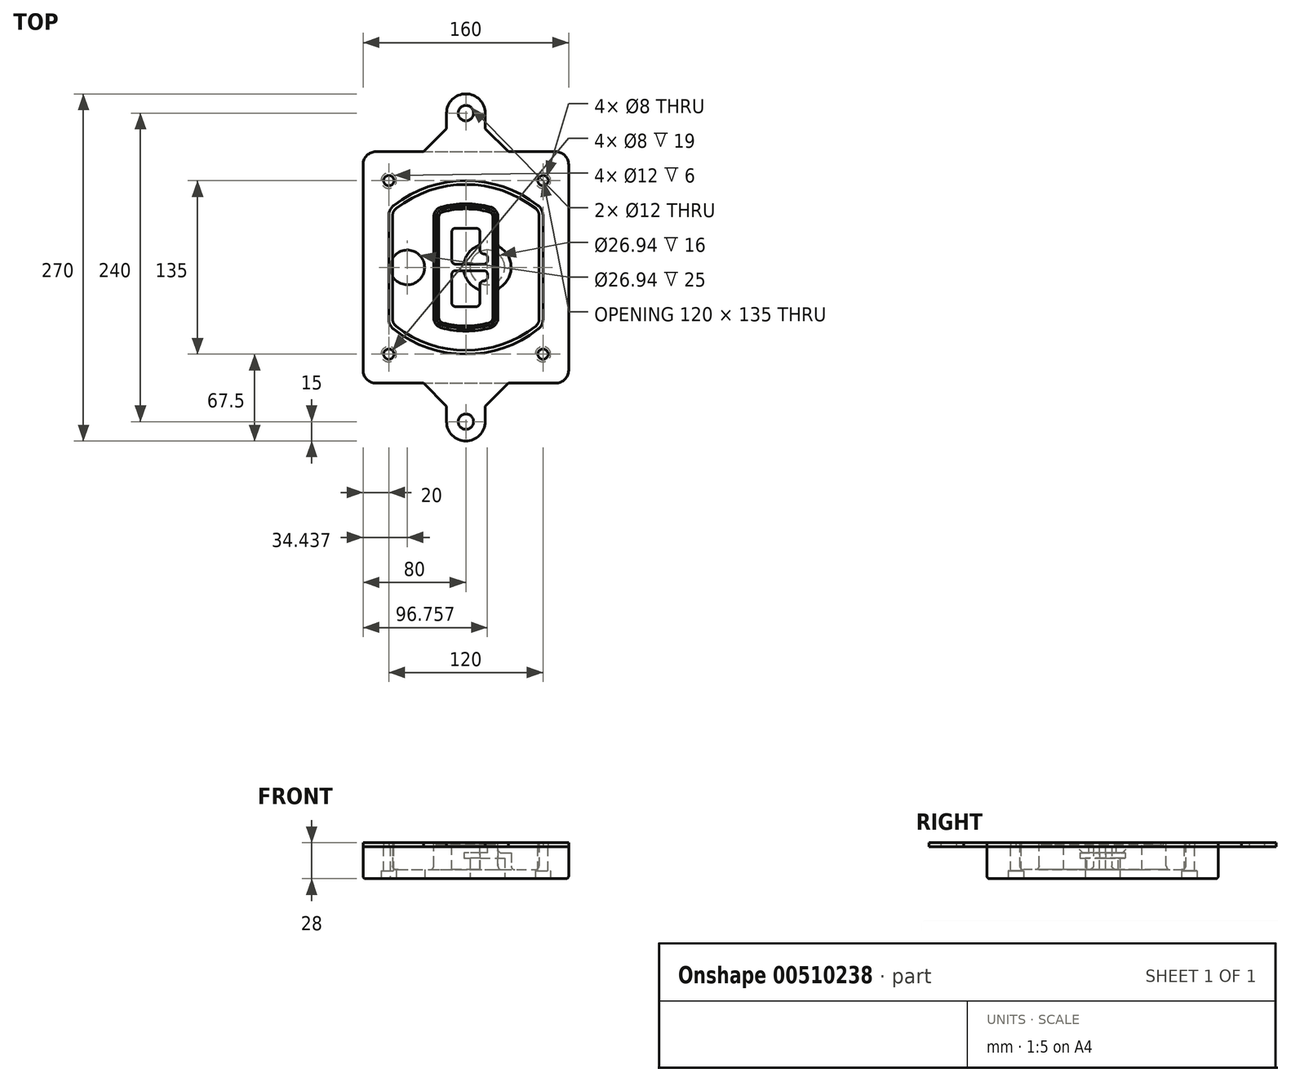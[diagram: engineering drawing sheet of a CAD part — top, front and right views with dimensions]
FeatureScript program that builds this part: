
annotation { "Feature Type Name" : "Feature", "Feature Type Description" : "" }
export const myFeature = defineFeature(function(context is Context, id is Id, definition is map)
    precondition{}
    {
        {
            var Q0;
            Q0=qCreatedBy(makeId("Top.planeOp"),FACE);
            var sketch = newSketch(context, id + "F0", { "sketchPlane" : qUnion([Q0])});
            skPoint(sketch, "E0.rect.middle", {"position": v(0, 0) * mm});
            skLineSegment(sketch, "E1.bottom", {"start": v(-70, -90) * mm, "end": v(70, -90) * mm});
            skLineSegment(sketch, "E1.top", {"start": v(-70, 90) * mm, "end": v(70, 90) * mm});
            skLineSegment(sketch, "E1.left", {"start": v(-80, -80) * mm, "end": v(-80, 80) * mm});
            skLineSegment(sketch, "E1.right", {"start": v(80, -80) * mm, "end": v(80, 80) * mm});
            skLineSegment(sketch, "E2", {"start": v(-80, 90) * mm, "end": v(80, -90) * mm, "construction": true});
            skLineSegment(sketch, "E3", {"start": v(80, 90) * mm, "end": v(-80, -90) * mm, "construction": true});
            skCircle(sketch, "E4", {"center": v(-60, 67.5) * mm, "radius": 4 * mm});
            skCircle(sketch, "E5", {"center": v(60, 67.5) * mm, "radius": 4 * mm});
            skCircle(sketch, "E6", {"center": v(60, -67.5) * mm, "radius": 4 * mm});
            skCircle(sketch, "E7", {"center": v(-60, -67.5) * mm, "radius": 4 * mm});
            skLineSegment(sketch, "E8", {"start": v(-60, 67.5) * mm, "end": v(60, 67.5) * mm, "construction": true});
            skLineSegment(sketch, "E9", {"start": v(60, 67.5) * mm, "end": v(60, -67.5) * mm, "construction": true});
            skLineSegment(sketch, "E10", {"start": v(60, -67.5) * mm, "end": v(-60, -67.5) * mm, "construction": true});
            skLineSegment(sketch, "E11", {"start": v(-60, -67.5) * mm, "end": v(-60, 67.5) * mm, "construction": true});
            skLineSegment(sketch, "E12", {"start": v(-60, 40.3) * mm, "end": v(-60, -40.3) * mm});
            skLineSegment(sketch, "E13", {"start": v(60, 40.3) * mm, "end": v(60, -40.3) * mm});
            skArc(sketch, "E14", {"start": v(56.15, 48.18) * mm, "mid": v(0, 67.5) * mm, "end": v(-56.15, 48.18) * mm});
            skArc(sketch, "E15", {"start": v(-56.15, -48.18) * mm, "mid": v(0, -67.5) * mm, "end": v(56.15, -48.18) * mm});
            skLineSegment(sketch, "E16", {"start": v(-60, 0) * mm, "end": v(60, 0) * mm, "construction": true});
            skPoint(sketch, "E17.visualSharp", {"position": v(-60, -45) * mm});
            skArc(sketch, "E17.filletArc", {"start": v(-60, -40.3) * mm, "mid": v(-58.99, -44.68) * mm, "end": v(-56.15, -48.18) * mm});
            skPoint(sketch, "E18.visualSharp", {"position": v(-60, 45) * mm});
            skArc(sketch, "E18.filletArc", {"start": v(-56.15, 48.18) * mm, "mid": v(-58.99, 44.68) * mm, "end": v(-60, 40.3) * mm});
            skPoint(sketch, "E19.visualSharp", {"position": v(60, 45) * mm});
            skArc(sketch, "E19.filletArc", {"start": v(60, 40.3) * mm, "mid": v(58.99, 44.68) * mm, "end": v(56.15, 48.18) * mm});
            skPoint(sketch, "E20.visualSharp", {"position": v(60, -45) * mm});
            skArc(sketch, "E20.filletArc", {"start": v(56.15, -48.18) * mm, "mid": v(58.99, -44.68) * mm, "end": v(60, -40.3) * mm});
            skPoint(sketch, "E21.visualSharp", {"position": v(-80, 90) * mm});
            skArc(sketch, "E21.filletArc", {"start": v(-70, 90) * mm, "mid": v(-77.07, 87.07) * mm, "end": v(-80, 80) * mm});
            skPoint(sketch, "E22.visualSharp", {"position": v(80, 90) * mm});
            skArc(sketch, "E22.filletArc", {"start": v(80, 80) * mm, "mid": v(77.07, 87.07) * mm, "end": v(70, 90) * mm});
            skPoint(sketch, "E23.visualSharp", {"position": v(80, -90) * mm});
            skArc(sketch, "E23.filletArc", {"start": v(70, -90) * mm, "mid": v(77.07, -87.07) * mm, "end": v(80, -80) * mm});
            skPoint(sketch, "E24.visualSharp", {"position": v(-80, -90) * mm});
            skArc(sketch, "E24.filletArc", {"start": v(-80, -80) * mm, "mid": v(-77.07, -87.07) * mm, "end": v(-70, -90) * mm});
            skArc(sketch, "E25.0", {"start": v(57, 40.3) * mm, "mid": v(56.3, 43.36) * mm, "end": v(54.3, 45.81) * mm});
            skLineSegment(sketch, "E25.1", {"start": v(57, 40.3) * mm, "end": v(57, -40.3) * mm});
            skArc(sketch, "E25.2", {"start": v(54.3, -45.81) * mm, "mid": v(56.3, -43.36) * mm, "end": v(57, -40.3) * mm});
            skArc(sketch, "E25.3", {"start": v(-54.3, -45.81) * mm, "mid": v(0, -64.5) * mm, "end": v(54.3, -45.81) * mm});
            skArc(sketch, "E25.4", {"start": v(-57, -40.3) * mm, "mid": v(-56.3, -43.36) * mm, "end": v(-54.3, -45.81) * mm});
            skArc(sketch, "E25.5", {"start": v(54.3, 45.81) * mm, "mid": v(0, 64.5) * mm, "end": v(-54.3, 45.81) * mm});
            skLineSegment(sketch, "E25.6", {"start": v(-57, 40.3) * mm, "end": v(-57, -40.3) * mm});
            skArc(sketch, "E25.7", {"start": v(-54.3, 45.81) * mm, "mid": v(-56.3, 43.36) * mm, "end": v(-57, 40.3) * mm});
            skArc(sketch, "E26.0", {"start": v(-58.62, 51.33) * mm, "mid": v(-62.58, 46.43) * mm, "end": v(-64, 40.3) * mm});
            skArc(sketch, "E26.1", {"start": v(58.62, 51.33) * mm, "mid": v(0, 71.5) * mm, "end": v(-58.62, 51.33) * mm});
            skArc(sketch, "E26.2", {"start": v(64, 40.3) * mm, "mid": v(62.58, 46.43) * mm, "end": v(58.62, 51.33) * mm});
            skLineSegment(sketch, "E26.3", {"start": v(64, 40.3) * mm, "end": v(64, -40.3) * mm});
            skArc(sketch, "E26.4", {"start": v(58.62, -51.33) * mm, "mid": v(62.58, -46.43) * mm, "end": v(64, -40.3) * mm});
            skLineSegment(sketch, "E26.5", {"start": v(-64, 40.3) * mm, "end": v(-64, -40.3) * mm});
            skArc(sketch, "E26.6", {"start": v(-58.62, -51.33) * mm, "mid": v(0, -71.5) * mm, "end": v(58.62, -51.33) * mm});
            skArc(sketch, "E26.7", {"start": v(-64, -40.3) * mm, "mid": v(-62.58, -46.43) * mm, "end": v(-58.62, -51.33) * mm});
            skSolve(sketch);
        }
        {
            var Q0;
            Q0=makeQuery(id+"F0.imprint","IMPRINT",FACE,{"disambiguationData":[TD([[makeQuery(id+"F0.imprint","IMPRINT",EDGE,{"derivedFrom":sQuery(id+"F0.wireOp",EDGE,"E1.bottom")}),1.0]])]});
            var Q1;
            Q1=makeQuery(id+"F0.imprint","IMPRINT",FACE,{"disambiguationData":[TD([[makeQuery(id+"F0.imprint","IMPRINT",EDGE,{"derivedFrom":sQuery(id+"F0.wireOp",EDGE,"E12")}),1.0]])]});
            var Q2;
            Q2=makeQuery(id+"F0.imprint","IMPRINT",FACE,{"disambiguationData":[TD([[makeQuery(id+"F0.imprint","IMPRINT",EDGE,{"derivedFrom":sQuery(id+"F0.wireOp",EDGE,"E25.0")}),1.0]])]});
            var Q3;
            Q3=makeQuery(id+"F0.imprint","IMPRINT",FACE,{"disambiguationData":[TD([[makeQuery(id+"F0.imprint","IMPRINT",EDGE,{"derivedFrom":sQuery(id+"F0.wireOp",EDGE,"E12")}),-1.0]])]});
            extrude(context, id + "F1", {"entities" : qUnion([Q0, Q1, Q2, Q3]), "oppositeDirection" : true, "depth" : 25 * mm});
        }
        {
            var Q0;
            Q0=makeQuery(id+"F0.imprint","IMPRINT",FACE,{"disambiguationData":[TD([[makeQuery(id+"F0.imprint","IMPRINT",EDGE,{"derivedFrom":sQuery(id+"F0.wireOp",EDGE,"E12")}),1.0]])]});
            extrude(context, id + "F2", {"entities" : qUnion([Q0]), "operationType" : NewBodyOperationType.ADD, "depth" : 3 * mm});
        }
        {
            var Q0;
            Q0=makeQuery(id+"F0.imprint","IMPRINT",FACE,{"disambiguationData":[TD([[makeQuery(id+"F0.imprint","IMPRINT",EDGE,{"derivedFrom":sQuery(id+"F0.wireOp",EDGE,"E25.0")}),1.0]])]});
            extrude(context, id + "F3", {"entities" : qUnion([Q0]), "operationType" : NewBodyOperationType.REMOVE, "oppositeDirection" : true, "depth" : 18 * mm});
        }
        {
            var Q0;
            Q0=makeQuery(id+"F2.opExtrude","CAP_FACE",FACE,{"disambiguationData":[OSD([sQuery(id+"F0.wireOp",EDGE,"E12"),sQuery(id+"F0.wireOp",EDGE,"E13"),sQuery(id+"F0.wireOp",EDGE,"E14"),sQuery(id+"F0.wireOp",EDGE,"E15"),sQuery(id+"F0.wireOp",EDGE,"E17.filletArc"),sQuery(id+"F0.wireOp",EDGE,"E18.filletArc"),sQuery(id+"F0.wireOp",EDGE,"E19.filletArc"),sQuery(id+"F0.wireOp",EDGE,"E20.filletArc"),sQuery(id+"F0.wireOp",EDGE,"E25.0"),sQuery(id+"F0.wireOp",EDGE,"E25.1"),sQuery(id+"F0.wireOp",EDGE,"E25.2"),sQuery(id+"F0.wireOp",EDGE,"E25.3"),sQuery(id+"F0.wireOp",EDGE,"E25.4"),sQuery(id+"F0.wireOp",EDGE,"E25.5"),sQuery(id+"F0.wireOp",EDGE,"E25.6"),sQuery(id+"F0.wireOp",EDGE,"E25.7")])],"isStart":false});
            var sketch = newSketch(context, id + "F4", { "sketchPlane" : qUnion([Q0])});
            skArc(sketch, "E27.0", {"start": v(-19.08, -46.97) * mm, "mid": v(0, -49.5) * mm, "end": v(19.08, -46.97) * mm});
            skArc(sketch, "E28.0", {"start": v(19.08, 46.97) * mm, "mid": v(0, 49.5) * mm, "end": v(-19.08, 46.97) * mm});
            skLineSegment(sketch, "E29", {"start": v(-25, 39.25) * mm, "end": v(-25, -39.25) * mm});
            skLineSegment(sketch, "E30", {"start": v(25, 39.25) * mm, "end": v(25, -39.25) * mm});
            skLineSegment(sketch, "E31", {"start": v(-25, 45.1) * mm, "end": v(25, 45.1) * mm, "construction": true});
            skLineSegment(sketch, "E32", {"start": v(-25, -45.1) * mm, "end": v(25, -45.1) * mm, "construction": true});
            skPoint(sketch, "E33.visualSharp", {"position": v(-25, 45.1) * mm});
            skArc(sketch, "E33.filletArc", {"start": v(-19.08, 46.97) * mm, "mid": v(-23.35, 44.11) * mm, "end": v(-25, 39.25) * mm});
            skPoint(sketch, "E34.visualSharp", {"position": v(25, 45.1) * mm});
            skArc(sketch, "E34.filletArc", {"start": v(25, 39.25) * mm, "mid": v(23.35, 44.11) * mm, "end": v(19.08, 46.97) * mm});
            skPoint(sketch, "E35.visualSharp", {"position": v(25, -45.1) * mm});
            skArc(sketch, "E35.filletArc", {"start": v(19.08, -46.97) * mm, "mid": v(23.35, -44.11) * mm, "end": v(25, -39.25) * mm});
            skPoint(sketch, "E36.visualSharp", {"position": v(-25, -45.1) * mm});
            skArc(sketch, "E36.filletArc", {"start": v(-25, -39.25) * mm, "mid": v(-23.35, -44.11) * mm, "end": v(-19.08, -46.97) * mm});
            skArc(sketch, "E37.0", {"start": v(54.3, 45.81) * mm, "mid": v(0, 64.5) * mm, "end": v(-54.3, 45.81) * mm});
            skArc(sketch, "E37.1", {"start": v(-54.3, 45.81) * mm, "mid": v(-56.3, 43.36) * mm, "end": v(-57, 40.3) * mm});
            skLineSegment(sketch, "E37.2", {"start": v(-57, 40.3) * mm, "end": v(-57, -40.3) * mm});
            skArc(sketch, "E37.3", {"start": v(-57, -40.3) * mm, "mid": v(-56.3, -43.36) * mm, "end": v(-54.3, -45.81) * mm});
            skArc(sketch, "E37.4", {"start": v(-54.3, -45.81) * mm, "mid": v(0, -64.5) * mm, "end": v(54.3, -45.81) * mm});
            skArc(sketch, "E37.5", {"start": v(54.3, -45.81) * mm, "mid": v(56.3, -43.36) * mm, "end": v(57, -40.3) * mm});
            skLineSegment(sketch, "E37.6", {"start": v(57, 40.3) * mm, "end": v(57, -40.3) * mm});
            skArc(sketch, "E37.7", {"start": v(57, 40.3) * mm, "mid": v(56.3, 43.36) * mm, "end": v(54.3, 45.81) * mm});
            skLineSegment(sketch, "E38.0", {"start": v(23, 39.25) * mm, "end": v(23, -39.25) * mm});
            skArc(sketch, "E38.1", {"start": v(18.56, -45.04) * mm, "mid": v(21.76, -42.9) * mm, "end": v(23, -39.25) * mm});
            skArc(sketch, "E38.2", {"start": v(-18.56, -45.04) * mm, "mid": v(0, -47.5) * mm, "end": v(18.56, -45.04) * mm});
            skArc(sketch, "E38.3", {"start": v(-23, -39.25) * mm, "mid": v(-21.76, -42.9) * mm, "end": v(-18.56, -45.04) * mm});
            skLineSegment(sketch, "E38.4", {"start": v(-23, 39.25) * mm, "end": v(-23, -39.25) * mm});
            skArc(sketch, "E38.5", {"start": v(23, 39.25) * mm, "mid": v(21.76, 42.9) * mm, "end": v(18.56, 45.04) * mm});
            skArc(sketch, "E38.6", {"start": v(-18.56, 45.04) * mm, "mid": v(-21.76, 42.9) * mm, "end": v(-23, 39.25) * mm});
            skArc(sketch, "E38.7", {"start": v(18.56, 45.04) * mm, "mid": v(0, 47.5) * mm, "end": v(-18.56, 45.04) * mm});
            skArc(sketch, "E39.0", {"start": v(21, 39.25) * mm, "mid": v(20.18, 41.68) * mm, "end": v(18.04, 43.1) * mm});
            skLineSegment(sketch, "E39.1", {"start": v(21, 39.25) * mm, "end": v(21, -39.25) * mm});
            skArc(sketch, "E39.2", {"start": v(18.04, -43.1) * mm, "mid": v(20.18, -41.68) * mm, "end": v(21, -39.25) * mm});
            skArc(sketch, "E39.3", {"start": v(-18.04, -43.1) * mm, "mid": v(0, -45.5) * mm, "end": v(18.04, -43.1) * mm});
            skArc(sketch, "E39.4", {"start": v(-21, -39.25) * mm, "mid": v(-20.18, -41.68) * mm, "end": v(-18.04, -43.1) * mm});
            skArc(sketch, "E39.5", {"start": v(18.04, 43.1) * mm, "mid": v(0, 45.5) * mm, "end": v(-18.04, 43.1) * mm});
            skLineSegment(sketch, "E39.6", {"start": v(-21, 39.25) * mm, "end": v(-21, -39.25) * mm});
            skArc(sketch, "E39.7", {"start": v(-18.04, 43.1) * mm, "mid": v(-20.18, 41.68) * mm, "end": v(-21, 39.25) * mm});
            skLineSegment(sketch, "E40", {"start": v(-25, 0) * mm, "end": v(25, 0) * mm, "construction": true});
            skLineSegment(sketch, "E41", {"start": v(-11, 5.5) * mm, "end": v(-11, 27.5) * mm});
            skLineSegment(sketch, "E42", {"start": v(-8, 30.5) * mm, "end": v(8, 30.5) * mm});
            skLineSegment(sketch, "E43", {"start": v(11, 27.5) * mm, "end": v(11, 13.5) * mm});
            skLineSegment(sketch, "E44", {"start": v(14, 10.5) * mm, "end": v(14, 10.5) * mm});
            skLineSegment(sketch, "E45", {"start": v(17, 7.5) * mm, "end": v(17, 5.5) * mm});
            skLineSegment(sketch, "E46", {"start": v(14, 2.5) * mm, "end": v(-8, 2.5) * mm});
            skPoint(sketch, "E47.visualSharp", {"position": v(-11, 30.5) * mm});
            skArc(sketch, "E47.filletArc", {"start": v(-8, 30.5) * mm, "mid": v(-10.12, 29.62) * mm, "end": v(-11, 27.5) * mm});
            skPoint(sketch, "E48.visualSharp", {"position": v(11, 30.5) * mm});
            skArc(sketch, "E48.filletArc", {"start": v(11, 27.5) * mm, "mid": v(10.12, 29.62) * mm, "end": v(8, 30.5) * mm});
            skPoint(sketch, "E49.visualSharp", {"position": v(11, 10.5) * mm});
            skArc(sketch, "E49.filletArc", {"start": v(11, 13.5) * mm, "mid": v(11.88, 11.38) * mm, "end": v(14, 10.5) * mm});
            skPoint(sketch, "E50.visualSharp", {"position": v(17, 10.5) * mm});
            skArc(sketch, "E50.filletArc", {"start": v(17, 7.5) * mm, "mid": v(16.12, 9.62) * mm, "end": v(14, 10.5) * mm});
            skPoint(sketch, "E51.visualSharp", {"position": v(17, 2.5) * mm});
            skArc(sketch, "E51.filletArc", {"start": v(14, 2.5) * mm, "mid": v(16.12, 3.38) * mm, "end": v(17, 5.5) * mm});
            skPoint(sketch, "E52.visualSharp", {"position": v(-11, 2.5) * mm});
            skArc(sketch, "E52.filletArc", {"start": v(-11, 5.5) * mm, "mid": v(-10.12, 3.38) * mm, "end": v(-8, 2.5) * mm});
            skLineSegment(sketch, "E53.0.MirrorCS", {"start": v(14, -2.5) * mm, "end": v(-8, -2.5) * mm});
            skArc(sketch, "E54.0.MirrorCS", {"start": v(-11, -5.5) * mm, "mid": v(-10.12, -3.38) * mm, "end": v(-8, -2.5) * mm});
            skLineSegment(sketch, "E55.0.MirrorCS", {"start": v(-11, -5.5) * mm, "end": v(-11, -27.5) * mm});
            skArc(sketch, "E56.0.MirrorCS", {"start": v(-8, -30.5) * mm, "mid": v(-10.12, -29.62) * mm, "end": v(-11, -27.5) * mm});
            skLineSegment(sketch, "E57.0.MirrorCS", {"start": v(-8, -30.5) * mm, "end": v(8, -30.5) * mm});
            skArc(sketch, "E58.0.MirrorCS", {"start": v(11, -27.5) * mm, "mid": v(10.12, -29.62) * mm, "end": v(8, -30.5) * mm});
            skLineSegment(sketch, "E59.0.MirrorCS", {"start": v(11, -27.5) * mm, "end": v(11, -13.5) * mm});
            skArc(sketch, "E60.0.MirrorCS", {"start": v(11, -13.5) * mm, "mid": v(11.88, -11.38) * mm, "end": v(14, -10.5) * mm});
            skArc(sketch, "E61.0.MirrorCS", {"start": v(17, -7.5) * mm, "mid": v(16.12, -9.62) * mm, "end": v(14, -10.5) * mm});
            skLineSegment(sketch, "E62.0.MirrorCS", {"start": v(17, -7.5) * mm, "end": v(17, -5.5) * mm});
            skArc(sketch, "E63.0.MirrorCS", {"start": v(14, -2.5) * mm, "mid": v(16.12, -3.38) * mm, "end": v(17, -5.5) * mm});
            skSolve(sketch);
        }
        {
            var Q0;
            Q0=makeQuery(id+"F4.imprint","IMPRINT",FACE,{"disambiguationData":[TD([[makeQuery(id+"F4.imprint","IMPRINT",EDGE,{"derivedFrom":sQuery(id+"F4.wireOp",EDGE,"E27.0")}),1.0]])]});
            var Q1;
            Q1=makeQuery(id+"F4.imprint","IMPRINT",FACE,{"disambiguationData":[TD([[makeQuery(id+"F4.imprint","IMPRINT",EDGE,{"derivedFrom":sQuery(id+"F4.wireOp",EDGE,"E38.0")}),-1.0]])]});
            var Q2;
            Q2=makeQuery(id+"F4.imprint","IMPRINT",FACE,{"disambiguationData":[TD([[makeQuery(id+"F4.imprint","IMPRINT",EDGE,{"derivedFrom":sQuery(id+"F4.wireOp",EDGE,"E39.0")}),1.0]])]});
            extrude(context, id + "F5", {"entities" : qUnion([Q0, Q1, Q2]), "operationType" : NewBodyOperationType.ADD, "endBound" : BoundingType.UP_TO_NEXT, "oppositeDirection" : true, "depth" : 25 * mm});
        }
        {
            var Q0;
            Q0=makeQuery(id+"F4.imprint","IMPRINT",FACE,{"disambiguationData":[TD([[makeQuery(id+"F4.imprint","IMPRINT",EDGE,{"derivedFrom":sQuery(id+"F4.wireOp",EDGE,"E38.0")}),-1.0]])]});
            extrude(context, id + "F6", {"entities" : qUnion([Q0]), "operationType" : NewBodyOperationType.REMOVE, "oppositeDirection" : true, "depth" : 2 * mm});
        }
        {
            var Q0;
            Q0=makeQuery(id+"F1.opExtrude","CAP_FACE",FACE,{"disambiguationData":[OSD([sQuery(id+"F0.wireOp",EDGE,"E1.bottom"),sQuery(id+"F0.wireOp",EDGE,"E1.top"),sQuery(id+"F0.wireOp",EDGE,"E1.left"),sQuery(id+"F0.wireOp",EDGE,"E1.right"),sQuery(id+"F0.wireOp",EDGE,"E4"),sQuery(id+"F0.wireOp",EDGE,"E5"),sQuery(id+"F0.wireOp",EDGE,"E6"),sQuery(id+"F0.wireOp",EDGE,"E7"),sQuery(id+"F0.wireOp",EDGE,"E21.filletArc"),sQuery(id+"F0.wireOp",EDGE,"E22.filletArc"),sQuery(id+"F0.wireOp",EDGE,"E23.filletArc"),sQuery(id+"F0.wireOp",EDGE,"E24.filletArc")])],"isStart":false});
            var sketch = newSketch(context, id + "F7", { "sketchPlane" : qUnion([Q0])});
            skCircle(sketch, "E64", {"center": v(16.76, 0) * mm, "radius": 13.47 * mm});
            skCircle(sketch, "E65", {"center": v(-45.56, 0) * mm, "radius": 13.47 * mm});
            skLineSegment(sketch, "E66", {"start": v(80, 0) * mm, "end": v(-80, 0) * mm});
            skCircle(sketch, "E67", {"center": v(16.76, 0) * mm, "radius": 18.47 * mm});
            skCircle(sketch, "E68", {"center": v(60, -67.5) * mm, "radius": 6 * mm});
            skCircle(sketch, "E69", {"center": v(-60, -67.5) * mm, "radius": 6 * mm});
            skCircle(sketch, "E70", {"center": v(-60, 67.5) * mm, "radius": 6 * mm});
            skCircle(sketch, "E71", {"center": v(60, 67.5) * mm, "radius": 6 * mm});
            skSolve(sketch);
        }
        {
            var Q0;
            {var subQ1=sQuery(id+"F7.wireOp",EDGE,"E66");var subQ4=sQuery(id+"F7.wireOp",EDGE,"E64");var subQ6=makeQuery(id+"F7.imprint","INTERSECT",VERTEX,{"disambiguationData":[OD(0.0)],"derivedFrom":[subQ4,subQ1]});Q0=makeQuery(id+"F7.imprint","IMPRINT",FACE,{"disambiguationData":[TD([[makeQuery(id+"F7.imprint","IMPRINT",EDGE,{"disambiguationData":[TD([[subQ6,-1.0]])],"derivedFrom":subQ4}),-1.0]])]});}
            var Q1;
            {var subQ0=sQuery(id+"F7.wireOp",EDGE,"E66");var subQ1=sQuery(id+"F7.wireOp",EDGE,"E64");var subQ3=makeQuery(id+"F7.imprint","INTERSECT",VERTEX,{"disambiguationData":[OD(0.0)],"derivedFrom":[subQ1,subQ0]});Q1=makeQuery(id+"F7.imprint","IMPRINT",FACE,{"disambiguationData":[TD([[makeQuery(id+"F7.imprint","IMPRINT",EDGE,{"disambiguationData":[TD([[subQ3,-1.0]])],"derivedFrom":subQ1}),1.0]])]});}
            var Q2;
            {var subQ0=sQuery(id+"F7.wireOp",EDGE,"E66");var subQ1=sQuery(id+"F7.wireOp",EDGE,"E64");var subQ3=makeQuery(id+"F7.imprint","INTERSECT",VERTEX,{"disambiguationData":[OD(0.0)],"derivedFrom":[subQ1,subQ0]});Q2=makeQuery(id+"F7.imprint","IMPRINT",FACE,{"disambiguationData":[TD([[makeQuery(id+"F7.imprint","IMPRINT",EDGE,{"disambiguationData":[TD([[subQ3,1.0]])],"derivedFrom":subQ1}),1.0]])]});}
            var Q3;
            {var subQ1=sQuery(id+"F7.wireOp",EDGE,"E66");var subQ4=sQuery(id+"F7.wireOp",EDGE,"E64");var subQ6=makeQuery(id+"F7.imprint","INTERSECT",VERTEX,{"disambiguationData":[OD(0.0)],"derivedFrom":[subQ4,subQ1]});Q3=makeQuery(id+"F7.imprint","IMPRINT",FACE,{"disambiguationData":[TD([[makeQuery(id+"F7.imprint","IMPRINT",EDGE,{"disambiguationData":[TD([[subQ6,1.0]])],"derivedFrom":subQ4}),-1.0]])]});}
            extrude(context, id + "F8", {"entities" : qUnion([Q0, Q1, Q2, Q3]), "operationType" : NewBodyOperationType.ADD, "oppositeDirection" : true, "depth" : 20 * mm});
        }
        {
            var Q0;
            {var subQ0=sQuery(id+"F7.wireOp",EDGE,"E66");var subQ1=sQuery(id+"F7.wireOp",EDGE,"E64");var subQ3=makeQuery(id+"F7.imprint","INTERSECT",VERTEX,{"disambiguationData":[OD(0.0)],"derivedFrom":[subQ1,subQ0]});Q0=makeQuery(id+"F7.imprint","IMPRINT",FACE,{"disambiguationData":[TD([[makeQuery(id+"F7.imprint","IMPRINT",EDGE,{"disambiguationData":[TD([[subQ3,-1.0]])],"derivedFrom":subQ1}),1.0]])]});}
            var Q1;
            {var subQ0=sQuery(id+"F7.wireOp",EDGE,"E66");var subQ1=sQuery(id+"F7.wireOp",EDGE,"E64");var subQ3=makeQuery(id+"F7.imprint","INTERSECT",VERTEX,{"disambiguationData":[OD(0.0)],"derivedFrom":[subQ1,subQ0]});Q1=makeQuery(id+"F7.imprint","IMPRINT",FACE,{"disambiguationData":[TD([[makeQuery(id+"F7.imprint","IMPRINT",EDGE,{"disambiguationData":[TD([[subQ3,1.0]])],"derivedFrom":subQ1}),1.0]])]});}
            extrude(context, id + "F9", {"entities" : qUnion([Q0, Q1]), "operationType" : NewBodyOperationType.REMOVE, "oppositeDirection" : true, "depth" : 16 * mm});
        }
        {
            var Q0;
            {var subQ0=sQuery(id+"F7.wireOp",EDGE,"E66");var subQ1=sQuery(id+"F7.wireOp",EDGE,"E65");var subQ3=makeQuery(id+"F7.imprint","INTERSECT",VERTEX,{"disambiguationData":[OD(0.0)],"derivedFrom":[subQ1,subQ0]});Q0=makeQuery(id+"F7.imprint","IMPRINT",FACE,{"disambiguationData":[TD([[makeQuery(id+"F7.imprint","IMPRINT",EDGE,{"disambiguationData":[TD([[subQ3,-1.0]])],"derivedFrom":subQ1}),1.0]])]});}
            var Q1;
            {var subQ0=sQuery(id+"F7.wireOp",EDGE,"E66");var subQ1=sQuery(id+"F7.wireOp",EDGE,"E65");var subQ3=makeQuery(id+"F7.imprint","INTERSECT",VERTEX,{"disambiguationData":[OD(0.0)],"derivedFrom":[subQ1,subQ0]});Q1=makeQuery(id+"F7.imprint","IMPRINT",FACE,{"disambiguationData":[TD([[makeQuery(id+"F7.imprint","IMPRINT",EDGE,{"disambiguationData":[TD([[subQ3,1.0]])],"derivedFrom":subQ1}),1.0]])]});}
            extrude(context, id + "F10", {"entities" : qUnion([Q0, Q1]), "operationType" : NewBodyOperationType.REMOVE, "oppositeDirection" : true, "depth" : 25 * mm});
        }
        {
            var Q0;
            Q0=makeQuery(id+"F7.imprint","IMPRINT",FACE,{"disambiguationData":[TD([[makeQuery(id+"F7.imprint","IMPRINT",EDGE,{"derivedFrom":sQuery(id+"F7.wireOp",EDGE,"E68")}),1.0]])]});
            var Q1;
            Q1=makeQuery(id+"F7.imprint","IMPRINT",FACE,{"disambiguationData":[TD([[makeQuery(id+"F7.imprint","IMPRINT",EDGE,{"derivedFrom":makeQuery(id+"F1.opExtrude","CAP_EDGE",EDGE,{"disambiguationData":[OSD([sQuery(id+"F0.wireOp",EDGE,"E5")])],"isStart":false})}),-1.0]])]});
            var Q2;
            Q2=makeQuery(id+"F7.imprint","IMPRINT",FACE,{"disambiguationData":[TD([[makeQuery(id+"F7.imprint","IMPRINT",EDGE,{"derivedFrom":sQuery(id+"F7.wireOp",EDGE,"E69")}),1.0]])]});
            var Q3;
            Q3=makeQuery(id+"F7.imprint","IMPRINT",FACE,{"disambiguationData":[TD([[makeQuery(id+"F7.imprint","IMPRINT",EDGE,{"derivedFrom":makeQuery(id+"F1.opExtrude","CAP_EDGE",EDGE,{"disambiguationData":[OSD([sQuery(id+"F0.wireOp",EDGE,"E4")])],"isStart":false})}),-1.0]])]});
            var Q4;
            Q4=makeQuery(id+"F7.imprint","IMPRINT",FACE,{"disambiguationData":[TD([[makeQuery(id+"F7.imprint","IMPRINT",EDGE,{"derivedFrom":sQuery(id+"F7.wireOp",EDGE,"E70")}),1.0]])]});
            var Q5;
            Q5=makeQuery(id+"F7.imprint","IMPRINT",FACE,{"disambiguationData":[TD([[makeQuery(id+"F7.imprint","IMPRINT",EDGE,{"derivedFrom":makeQuery(id+"F1.opExtrude","CAP_EDGE",EDGE,{"disambiguationData":[OSD([sQuery(id+"F0.wireOp",EDGE,"E7")])],"isStart":false})}),-1.0]])]});
            var Q6;
            Q6=makeQuery(id+"F7.imprint","IMPRINT",FACE,{"disambiguationData":[TD([[makeQuery(id+"F7.imprint","IMPRINT",EDGE,{"derivedFrom":sQuery(id+"F7.wireOp",EDGE,"E71")}),1.0]])]});
            var Q7;
            Q7=makeQuery(id+"F7.imprint","IMPRINT",FACE,{"disambiguationData":[TD([[makeQuery(id+"F7.imprint","IMPRINT",EDGE,{"derivedFrom":makeQuery(id+"F1.opExtrude","CAP_EDGE",EDGE,{"disambiguationData":[OSD([sQuery(id+"F0.wireOp",EDGE,"E6")])],"isStart":false})}),-1.0]])]});
            extrude(context, id + "F11", {"entities" : qUnion([Q0, Q1, Q2, Q3, Q4, Q5, Q6, Q7]), "operationType" : NewBodyOperationType.REMOVE, "oppositeDirection" : true, "depth" : 6 * mm});
        }
        {
            var Q0;
            Q0=makeQuery(id+"F9.boolean.opBoolean","COPY",FACE,{"derivedFrom":makeQuery(id+"F9.opExtrude","CAP_FACE",FACE,{"disambiguationData":[OSD([sQuery(id+"F7.wireOp",EDGE,"E64")])],"isStart":false})});
            var sketch = newSketch(context, id + "F12", { "sketchPlane" : qUnion([Q0])});
            skArc(sketch, "E72.0", {"start": v(11, 17.55) * mm, "mid": v(2.57, 11.82) * mm, "end": v(-1.54, 2.5) * mm});
            skArc(sketch, "E72.1", {"start": v(-1.54, -2.5) * mm, "mid": v(2.57, -11.82) * mm, "end": v(11, -17.55) * mm});
            skLineSegment(sketch, "E73", {"start": v(-1.54, -2.5) * mm, "end": v(14, -2.5) * mm});
            skLineSegment(sketch, "E74.0", {"start": v(14, 2.5) * mm, "end": v(-1.54, 2.5) * mm});
            skArc(sketch, "E74.1", {"start": v(14, 2.5) * mm, "mid": v(16.12, 3.38) * mm, "end": v(17, 5.5) * mm});
            skLineSegment(sketch, "E74.2", {"start": v(17, 7.5) * mm, "end": v(17, 5.5) * mm});
            skArc(sketch, "E74.3", {"start": v(17, 7.5) * mm, "mid": v(16.12, 9.62) * mm, "end": v(14, 10.5) * mm});
            skArc(sketch, "E74.4", {"start": v(11, 13.5) * mm, "mid": v(11.88, 11.38) * mm, "end": v(14, 10.5) * mm});
            skLineSegment(sketch, "E74.5", {"start": v(11, 17.55) * mm, "end": v(11, 13.5) * mm});
            skLineSegment(sketch, "E74.7", {"start": v(14, -2.5) * mm, "end": v(-1.54, -2.5) * mm});
            skArc(sketch, "E74.8", {"start": v(14, -2.5) * mm, "mid": v(16.12, -3.38) * mm, "end": v(17, -5.5) * mm});
            skLineSegment(sketch, "E74.9", {"start": v(17, -7.5) * mm, "end": v(17, -5.5) * mm});
            skArc(sketch, "E74.10", {"start": v(17, -7.5) * mm, "mid": v(16.12, -9.62) * mm, "end": v(14, -10.5) * mm});
            skArc(sketch, "E74.11", {"start": v(11, -13.5) * mm, "mid": v(11.88, -11.38) * mm, "end": v(14, -10.5) * mm});
            skLineSegment(sketch, "E74.12", {"start": v(11, -17.55) * mm, "end": v(11, -13.5) * mm});
            skPoint(sketch, "E75.orphan", {"position": v(11, -27.5) * mm});
            skPoint(sketch, "E76.orphan", {"position": v(-8, -2.5) * mm});
            skPoint(sketch, "E77.orphan", {"position": v(-8, 2.5) * mm});
            skPoint(sketch, "E78.orphan", {"position": v(11, 27.5) * mm});
            skSolve(sketch);
        }
        {
            var Q0;
            {var subQ7=sQuery(id+"F12.wireOp",EDGE,"E72.0");var subQ14=sQuery(id+"F12.wireOp",EDGE,"E72.1");var subQ16=sQuery(id+"F12.wireOp",EDGE,"E74.1");var subQ18=sQuery(id+"F12.wireOp",EDGE,"E74.8");Q0=qUnion([makeQuery(id+"F12.imprint","IMPRINT",FACE,{"disambiguationData":[TD([[makeQuery(id+"F12.imprint","IMPRINT",EDGE,{"derivedFrom":subQ7}),1.0]])]}),makeQuery(id+"F12.imprint","IMPRINT",FACE,{"disambiguationData":[TD([[makeQuery(id+"F12.imprint","IMPRINT",EDGE,{"derivedFrom":subQ14}),1.0]])]}),makeQuery(id+"F12.imprint","IMPRINT",FACE,{"disambiguationData":[TD([[makeQuery(id+"F12.imprint","IMPRINT",EDGE,{"derivedFrom":subQ16}),1.0]])]}),makeQuery(id+"F12.imprint","IMPRINT",FACE,{"disambiguationData":[TD([[makeQuery(id+"F12.imprint","IMPRINT",EDGE,{"derivedFrom":subQ18}),-1.0]])]})]);}
            var Q1;
            Q1=makeQuery(id+"F5.boolean.opBoolean","SPLIT",FACE,{"disambiguationData":[TD([makeQuery(id+"F5.opExtrude","SWEPT_FACE",FACE,{"disambiguationData":[OSD([sQuery(id+"F4.wireOp",EDGE,"E41")])]})])],"derivedFrom":makeQuery(id+"F3.boolean.opBoolean","COPY",FACE,{"derivedFrom":makeQuery(id+"F3.opExtrude","CAP_FACE",FACE,{"disambiguationData":[OSD([sQuery(id+"F0.wireOp",EDGE,"E25.0"),sQuery(id+"F0.wireOp",EDGE,"E25.1"),sQuery(id+"F0.wireOp",EDGE,"E25.2"),sQuery(id+"F0.wireOp",EDGE,"E25.3"),sQuery(id+"F0.wireOp",EDGE,"E25.4"),sQuery(id+"F0.wireOp",EDGE,"E25.5"),sQuery(id+"F0.wireOp",EDGE,"E25.6"),sQuery(id+"F0.wireOp",EDGE,"E25.7")])],"isStart":false})})});
            extrude(context, id + "F13", {"entities" : qUnion([Q0]), "operationType" : NewBodyOperationType.REMOVE, "endBound" : BoundingType.UP_TO_SURFACE, "endBoundEntityFace" : qUnion([Q1]), "depth" : 25 * mm});
        }
        {
            var Q0;
            Q0=makeQuery(id+"F3.boolean.opBoolean","COPY",EDGE,{"derivedFrom":makeQuery(id+"F3.opExtrude","CAP_EDGE",EDGE,{"disambiguationData":[OSD([sQuery(id+"F0.wireOp",EDGE,"E25.6")])],"isStart":false})});
            var Q1;
            Q1=makeQuery(id+"F8.boolean.opBoolean","INTERSECT",EDGE,{"derivedFrom":[makeQuery(id+"F5.opExtrude","SWEPT_FACE",FACE,{"disambiguationData":[OSD([sQuery(id+"F4.wireOp",EDGE,"E30")])]}),makeQuery(id+"F8.opExtrude","CAP_FACE",FACE,{"disambiguationData":[OSD([sQuery(id+"F7.wireOp",EDGE,"E67")])],"isStart":false})]});
            var Q2;
            Q2=makeQuery(id+"F8.boolean.opBoolean","INTERSECT",EDGE,{"disambiguationData":[OD(1.0)],"derivedFrom":[makeQuery(id+"F5.opExtrude","SWEPT_FACE",FACE,{"disambiguationData":[OSD([sQuery(id+"F4.wireOp",EDGE,"E30")])]}),makeQuery(id+"F8.opExtrude","SWEPT_FACE",FACE,{"disambiguationData":[OSD([sQuery(id+"F7.wireOp",EDGE,"E67")])]})]});
            var Q3;
            {var subQ0=sQuery(id+"F4.wireOp",EDGE,"E30");Q3=makeQuery(id+"F8.boolean.opBoolean","SPLIT",EDGE,{"disambiguationData":[TD([makeQuery(id+"F5.opExtrude","SWEPT_FACE",FACE,{"disambiguationData":[OSD([sQuery(id+"F4.wireOp",EDGE,"E35.filletArc")])]})])],"derivedFrom":makeQuery(id+"F5.opExtrude","CAP_EDGE",EDGE,{"disambiguationData":[OSD([subQ0])],"isStart":false})});}
            var Q4;
            {var subQ0=sQuery(id+"F0.wireOp",EDGE,"E25.7");var subQ1=sQuery(id+"F0.wireOp",EDGE,"E25.1");var subQ2=sQuery(id+"F0.wireOp",EDGE,"E25.6");var subQ3=sQuery(id+"F0.wireOp",EDGE,"E25.5");var subQ4=sQuery(id+"F0.wireOp",EDGE,"E25.4");var subQ5=sQuery(id+"F0.wireOp",EDGE,"E25.0");var subQ6=sQuery(id+"F0.wireOp",EDGE,"E25.2");var subQ7=sQuery(id+"F0.wireOp",EDGE,"E25.3");Q4=makeQuery(id+"F8.boolean.opBoolean","INTERSECT",EDGE,{"derivedFrom":[makeQuery(id+"F5.boolean.opBoolean","SPLIT",FACE,{"disambiguationData":[TD([makeQuery(id+"F2.opExtrude","SWEPT_FACE",FACE,{"disambiguationData":[OSD([subQ5])]})])],"derivedFrom":makeQuery(id+"F3.boolean.opBoolean","COPY",FACE,{"derivedFrom":makeQuery(id+"F3.opExtrude","CAP_FACE",FACE,{"disambiguationData":[OSD([subQ5,subQ1,subQ6,subQ7,subQ4,subQ3,subQ2,subQ0])],"isStart":false})})}),makeQuery(id+"F8.opExtrude","SWEPT_FACE",FACE,{"disambiguationData":[OSD([sQuery(id+"F7.wireOp",EDGE,"E67")])]})]});}
            var Q5;
            Q5=makeQuery(id+"F8.boolean.opBoolean","INTERSECT",EDGE,{"disambiguationData":[OD(0.0)],"derivedFrom":[makeQuery(id+"F5.opExtrude","SWEPT_FACE",FACE,{"disambiguationData":[OSD([sQuery(id+"F4.wireOp",EDGE,"E30")])]}),makeQuery(id+"F8.opExtrude","SWEPT_FACE",FACE,{"disambiguationData":[OSD([sQuery(id+"F7.wireOp",EDGE,"E67")])]})]});
            fillet(context, id + "F14", {"entities" : qUnion([Q0, Q1, Q2, Q3, Q4, Q5]), "radius" : 3 * mm, "tangentPropagation" : true, "allowEdgeOverflow" : false});
        }
        {
            var Q0;
            Q0=makeQuery(id+"F1.opExtrude","CAP_EDGE",EDGE,{"disambiguationData":[OSD([sQuery(id+"F0.wireOp",EDGE,"E1.bottom")])],"isStart":false});
            fillet(context, id + "F15", {"entities" : qUnion([Q0]), "radius" : 2 * mm, "tangentPropagation" : true, "allowEdgeOverflow" : false});
        }
        {
            var Q0;
            Q0=qCreatedBy(makeId("Top.planeOp"),FACE);
            var sketch = newSketch(context, id + "F16", { "sketchPlane" : qUnion([Q0])});
            skArc(sketch, "E79.0", {"start": v(-70, 90) * mm, "mid": v(-77.07, 87.07) * mm, "end": v(-80, 80) * mm});
            skLineSegment(sketch, "E79.1", {"start": v(-80, -80) * mm, "end": v(-80, 80) * mm});
            skArc(sketch, "E79.2", {"start": v(-80, -80) * mm, "mid": v(-77.07, -87.07) * mm, "end": v(-70, -90) * mm});
            skLineSegment(sketch, "E79.3", {"start": v(-70, -90) * mm, "end": v(70, -90) * mm});
            skArc(sketch, "E79.4", {"start": v(70, -90) * mm, "mid": v(77.07, -87.07) * mm, "end": v(80, -80) * mm});
            skLineSegment(sketch, "E79.5", {"start": v(80, -80) * mm, "end": v(80, 80) * mm});
            skArc(sketch, "E79.6", {"start": v(80, 80) * mm, "mid": v(77.07, 87.07) * mm, "end": v(70, 90) * mm});
            skLineSegment(sketch, "E79.7", {"start": v(-70, 90) * mm, "end": v(70, 90) * mm});
            skArc(sketch, "E79.8", {"start": v(56.15, 48.18) * mm, "mid": v(0, 67.5) * mm, "end": v(-56.15, 48.18) * mm});
            skArc(sketch, "E79.9", {"start": v(-56.15, 48.18) * mm, "mid": v(-58.99, 44.68) * mm, "end": v(-60, 40.3) * mm});
            skLineSegment(sketch, "E79.10", {"start": v(-60, 40.3) * mm, "end": v(-60, -40.3) * mm});
            skArc(sketch, "E79.11", {"start": v(-60, -40.3) * mm, "mid": v(-58.99, -44.68) * mm, "end": v(-56.15, -48.18) * mm});
            skArc(sketch, "E79.12", {"start": v(-56.15, -48.18) * mm, "mid": v(0, -67.5) * mm, "end": v(56.15, -48.18) * mm});
            skArc(sketch, "E79.13", {"start": v(56.15, -48.18) * mm, "mid": v(58.99, -44.68) * mm, "end": v(60, -40.3) * mm});
            skLineSegment(sketch, "E79.14", {"start": v(60, 40.3) * mm, "end": v(60, -40.3) * mm});
            skArc(sketch, "E79.15", {"start": v(60, 40.3) * mm, "mid": v(58.99, 44.68) * mm, "end": v(56.15, 48.18) * mm});
            skCircle(sketch, "E79.16", {"center": v(60, 67.5) * mm, "radius": 4 * mm});
            skCircle(sketch, "E79.17", {"center": v(-60, 67.5) * mm, "radius": 4 * mm});
            skCircle(sketch, "E79.18", {"center": v(-60, -67.5) * mm, "radius": 4 * mm});
            skCircle(sketch, "E79.19", {"center": v(60, -67.5) * mm, "radius": 4 * mm});
            skLineSegment(sketch, "E80", {"start": v(0, 90) * mm, "end": v(0, 120) * mm, "construction": true});
            skPoint(sketch, "E80.endSnap0", {"position": v(0, 90) * mm});
            skCircle(sketch, "E81", {"center": v(0, 120) * mm, "radius": 6 * mm});
            skArc(sketch, "E82", {"start": v(15, 120) * mm, "mid": v(0, 135) * mm, "end": v(-15, 120) * mm});
            skLineSegment(sketch, "E83", {"start": v(-15, 120) * mm, "end": v(-15, 108) * mm});
            skLineSegment(sketch, "E84", {"start": v(15, 120) * mm, "end": v(15, 108) * mm});
            skLineSegment(sketch, "E85", {"start": v(-15, 108) * mm, "end": v(-33, 90) * mm});
            skLineSegment(sketch, "E86", {"start": v(15, 108) * mm, "end": v(33, 90) * mm});
            skLineSegment(sketch, "E87", {"start": v(-80, 0) * mm, "end": v(80, 0) * mm, "construction": true});
            skLineSegment(sketch, "E88.MirrorCS", {"start": v(0, -90) * mm, "end": v(0, -120) * mm, "construction": true});
            skArc(sketch, "E89.MirrorCS", {"start": v(15, -120) * mm, "mid": v(0, -135) * mm, "end": v(-15, -120) * mm});
            skLineSegment(sketch, "E90.MirrorCS", {"start": v(15, -120) * mm, "end": v(15, -108) * mm});
            skLineSegment(sketch, "E91.MirrorCS", {"start": v(-15, -120) * mm, "end": v(-15, -108) * mm});
            skPoint(sketch, "E92.MirrorP", {"position": v(0, -90) * mm});
            skCircle(sketch, "E93.MirrorC", {"center": v(0, -120) * mm, "radius": 6 * mm});
            skLineSegment(sketch, "E94.MirrorCS", {"start": v(-15, -108) * mm, "end": v(-33, -90) * mm});
            skLineSegment(sketch, "E95.MirrorCS", {"start": v(15, -108) * mm, "end": v(33, -90) * mm});
            skSolve(sketch);
        }
        {
            var Q0;
            Q0 = qSketchRegion(id + "F16", true);
            var Q1;
            Q1=makeQuery(id+"F2.opExtrude","CAP_FACE",FACE,{"disambiguationData":[OSD([sQuery(id+"F0.wireOp",EDGE,"E12"),sQuery(id+"F0.wireOp",EDGE,"E13"),sQuery(id+"F0.wireOp",EDGE,"E14"),sQuery(id+"F0.wireOp",EDGE,"E15"),sQuery(id+"F0.wireOp",EDGE,"E17.filletArc"),sQuery(id+"F0.wireOp",EDGE,"E18.filletArc"),sQuery(id+"F0.wireOp",EDGE,"E19.filletArc"),sQuery(id+"F0.wireOp",EDGE,"E20.filletArc"),sQuery(id+"F0.wireOp",EDGE,"E25.0"),sQuery(id+"F0.wireOp",EDGE,"E25.1"),sQuery(id+"F0.wireOp",EDGE,"E25.2"),sQuery(id+"F0.wireOp",EDGE,"E25.3"),sQuery(id+"F0.wireOp",EDGE,"E25.4"),sQuery(id+"F0.wireOp",EDGE,"E25.5"),sQuery(id+"F0.wireOp",EDGE,"E25.6"),sQuery(id+"F0.wireOp",EDGE,"E25.7")])],"isStart":false});
            extrude(context, id + "F17", {"entities" : qUnion([Q0]), "endBound" : BoundingType.UP_TO_SURFACE, "endBoundEntityFace" : qUnion([Q1]), "depth" : 25 * mm});
        }
    });
